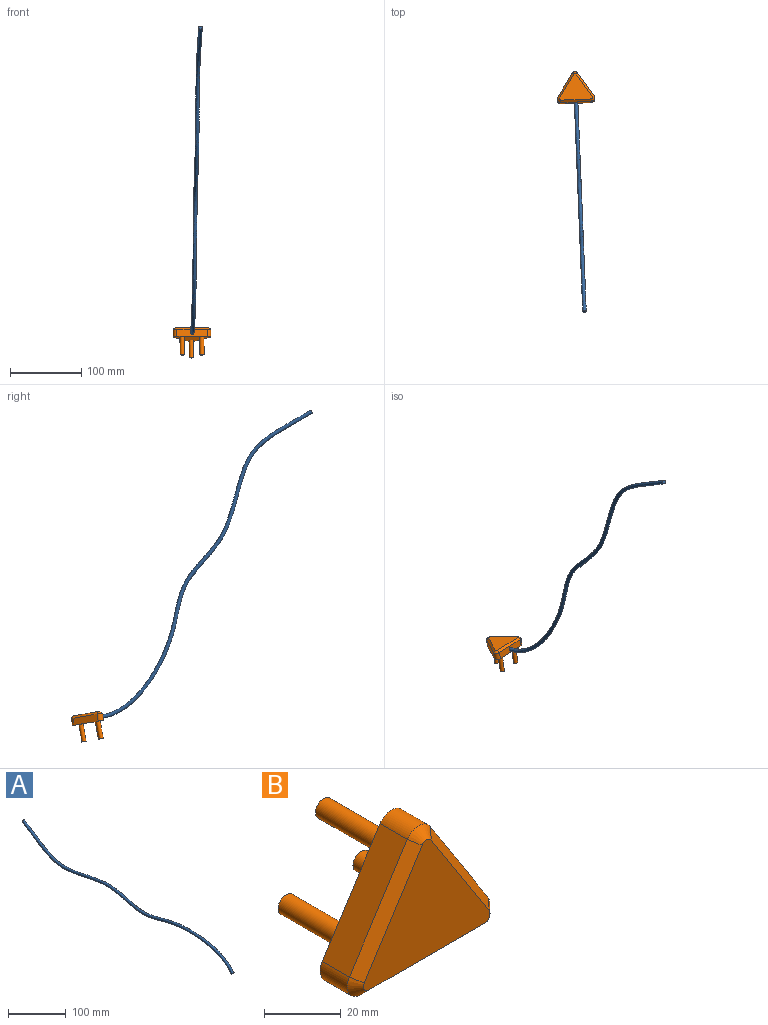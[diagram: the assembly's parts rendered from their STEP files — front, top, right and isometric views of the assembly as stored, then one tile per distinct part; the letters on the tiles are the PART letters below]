
ASSEMBLY  parts=2 mates=1
PART A: 3 faces, bbox 10x517.7x71.1 mm
  f0: plane 5x4.23mm, normal (0,0.85,0.53), area 19.6mm2, adj f2
  f1: plane 5x3.99mm, normal (0,-0.6,-0.8), area 19.6mm2, adj f2
  f2: bspline ~517.66x71.15mm, area 8513mm2, adj f0,f1
PART B: 20 faces, bbox 52.6x38x43.3 mm
  f0: plane 46.63x37.28mm, normal (0,-1,0), area 965.4mm2, adj f1,f2,f3,f4,f5,f6
  f1: plane 34.9x23.84mm, normal (-0.6,-0.71,0.38), area 167.7mm2, adj f0,f2,f6,f12
  f2: cone r=5mm half-angle=45deg, axis (0,1,0), area 31.8mm2, adj f0,f1,f3,f11
  f3: plane 42.63x3mm, normal (0,-0.71,-0.71), area 180.9mm2, adj f0,f2,f4,f10
  f4: cone r=5mm half-angle=45deg, axis (0,1,0), area 31.8mm2, adj f0,f3,f5,f9
  f5: plane 34.9x23.84mm, normal (0.6,-0.71,0.38), area 167.7mm2, adj f0,f4,f6,f8
  f6: cone r=5mm half-angle=45deg, axis (0,1,0), area 29.7mm2, adj f0,f1,f5,f7
  f7: cylinder r=5mm len=10mm, axis (0,-1,0), area 100.1mm2, adj f6,f8,f12,f13
  f8: plane 33.28x21.32mm, normal (0.84,0,0.54), area 395.2mm2, adj f5,f7,f9,f13
  f9: cylinder r=5mm len=10mm, axis (0,-1,0), area 107mm2, adj f4,f8,f10,f13
  f10: plane 42.63x10mm, normal (0,0,-1), area 426.3mm2, adj f3,f9,f11,f13
  f11: cylinder r=5mm len=10mm, axis (0,-1,0), area 107mm2, adj f2,f10,f12,f13
  f12: plane 33.28x21.32mm, normal (-0.84,0,0.54), area 395.2mm2, adj f1,f7,f11,f13
  f13: plane 52.63x43.28mm, normal (0,1,0), area 1311.6mm2, adj f7,f8,f9,f10,f11,f12,f14,f16
  f14: cylinder r=3mm len=25mm, axis (0,-1,0), area 471.2mm2, adj f13,f15
  f15: plane 6x6mm, normal (0,1,0), area 28.3mm2, adj f14
  f16: cylinder r=3mm len=25mm, axis (0,-1,0), area 471.2mm2, adj f13,f17
  f17: plane 6x6mm, normal (0,1,0), area 28.3mm2, adj f16
  f18: cylinder r=3mm len=25mm, axis (0,-1,0), area 471.2mm2, adj f13,f19
  f19: plane 6x6mm, normal (0,1,0), area 28.3mm2, adj f18
PLACE A rot(axis=(1,0.02,0.01),117deg) t=(25.11,-206.33,287.59)mm
PLACE B rot(axis=(-1,-0.02,0.02),100deg) t=(9.85,-22.88,43.77)mm
MATE fastened A.f1 <-> B.f10  axis (-0.04,0.98,-0.17) through (9.89,-23.75,38.85)mm
